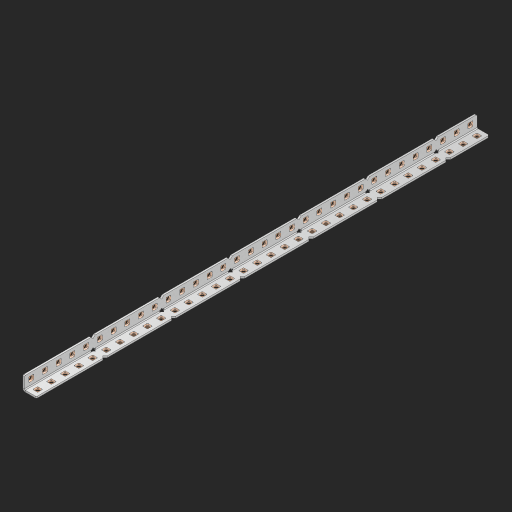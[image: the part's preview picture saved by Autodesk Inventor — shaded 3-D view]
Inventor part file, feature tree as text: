
AUTODESK INVENTOR PART (.ipt)
format: ipt  version: 2023 (Build 270158000, 158)  size: 1,092,096 bytes
history: native  units: in
note: dims shown in document units (in); Inventor stores cm internally (conversion verified against a paired STEP export)
features: other x72, extrude x67, sheet_metal_op x8, sketch x5, pattern_linear x1, mirror x1, chamfer x1
ambient origin geometry x8: Origin, YZ Plane, XZ Plane, XY Plane, X Axis, Y Axis, Z Axis, Center Point
bodies: Solid1 (feature_tree), Body (feature_tree)
feature tree (155):
  sheet_metal_op  "Flanges"
  sheet_metal_op  "Body Pattern"
  other  "Arc Length"
  pattern_linear  "Notch Pattern"  Spacing1=0.125in  [1 undecoded]
  other  "Diagonal Plane"
  mirror  "Everything Mirrored"
  chamfer  "End Chamfer"
  sketch  "Sketch1"  dims[d0=0.5in]
  other  "Plate1"
  sketch  "Sketch2"  dims[d1=16.5in]
  other  "Plate2"
  sheet_metal_op  "Bend1"
  sheet_metal_op  "Corner1"
  sketch  "Sketch8"  dims[d2=0.0625in]
  sketch  "Sketch9"  dims[d3=0.0625in]
  other  "Srf91"
  sheet_metal_op  "Body Pattern Sketch"
  other  "Srf92"
  sketch  "Sketch13"  dims[d4=0.0312in d5=0.125in d6=0.0625in d7=0.5in d8=90.0deg d9=0.0312in d10=0.25in d11=0.0625in d12=0.0625in d49=0.182in d50=0.02in d52=0.25in d53=0.0625in d54=0.0in d55=0.172in d56=1.0in d57=0.0in d85=0.1473in d86=0.1782in d89=0.0625in d90=0.0in d91=0.04in d92=0.0491in d95=2.5in d96=0.04in d97=0.25in d98=45.0deg d123=0.204in d126=0.0491in d127=0.1473in d128=0.08in d129=0.04in d130=2.5in d131=12.9921in d133=0.5in d134=0.3937in d136=1.0in]
  other  "Srf856"
  other  "Srf857"
  other  "Srf858"
  other  "Srf859"
  other  "Srf860"
  other  "Srf861"
  other  "Srf1275"
  other  "Srf1276"
  other  "Srf1278"
  other  "Srf1279"
  other  "Srf1280"
  other  "Srf1281"
  other  "Srf1282"
  other  "Srf1283"
  other  "Srf1383"
  other  "Srf1384"
  other  "Srf1385"
  other  "Srf1386"
  other  "Srf1387"
  other  "Srf1388"
  other  "Srf1389"
  other  "Srf1390"
  other  "Srf1391"
  other  "Srf1392"
  other  "Srf1393"
  other  "Srf1394"
  other  "Srf1395"
  other  "Srf1396"
  other  "Srf1397"
  other  "Srf1398"
  other  "Srf1399"
  other  "Srf1400"
  other  "Srf1401"
  other  "Srf1402"
  other  "Srf1403"
  other  "Srf1404"
  other  "Srf1405"
  other  "Srf1406"
  other  "Srf1407"
  other  "Srf1408"
  other  "Srf1475"
  other  "Srf1476"
  other  "Srf1477"
  other  "Srf1478"
  other  "Srf1479"
  other  "Srf1480"
  other  "Srf1481"
  other  "Srf1482"
  other  "Srf1483"
  other  "Srf1484"
  other  "Srf1485"
  other  "Srf1486"
  other  "Srf1487"
  other  "Srf1488"
  other  "Srf1489"
  other  "Srf1490"
  other  "Srf1491"
  other  "Srf1492"
  other  "Srf1493"
  other  "Srf1494"
  other  "Srf1495"
  other  "Srf1496"
  other  "Srf1497"
  other  "Srf1498"
  other  "Srf1499"
  other  "Srf1500"
  sheet_metal_op  "Body Stamp"
  sheet_metal_op  "Body Circle"
  sheet_metal_op  "Notch"
  extrude  "ExtrusionSrf92"  Depth=0.0625in
  extrude  "ExtrusionSrf856"  Depth=0.5in TaperAngle=90.0deg
  extrude  "ExtrusionSrf857"  Depth=0.25in
  extrude  "ExtrusionSrf858"  Depth=0.0625in
  extrude  "ExtrusionSrf859"  Depth=0.0625in
  extrude  "ExtrusionSrf860"  Depth=0.3937in
  extrude  "ExtrusionSrf861"  Depth=0.02in
  extrude  "ExtrusionSrf1275"  Depth=0.25in
  extrude  "ExtrusionSrf1276"  Depth=0.0625in
  extrude  "ExtrusionSrf1277"  TaperAngle=0.0deg  [1 undecoded]
  extrude  "ExtrusionSrf1278"  Depth=0.3937in
  extrude  "ExtrusionSrf1279"  Depth=0.3937in TaperAngle=0.0deg
  extrude  "ExtrusionSrf1280"  Depth=0.3937in
  extrude  "ExtrusionSrf1281"  Depth=0.3937in
  extrude  "ExtrusionSrf1282"  Depth=0.0625in
  extrude  "ExtrusionSrf1383"  Depth=0.3937in TaperAngle=0.0deg
  extrude  "ExtrusionSrf1384"  Depth=0.3937in
  extrude  "ExtrusionSrf1385"  Depth=0.25in TaperAngle=45.0deg
  extrude  "ExtrusionSrf1386"  Depth=0.3937in
  extrude  "ExtrusionSrf1387"  Depth=0.3937in
  extrude  "ExtrusionSrf1388"  Depth=0.3937in
  extrude  "ExtrusionSrf1389"  Depth=0.3937in
  extrude  "ExtrusionSrf1390"  Depth=0.3937in
  extrude  "ExtrusionSrf1391"  Depth=0.3937in
  extrude  "ExtrusionSrf1392"  Depth=0.3937in
  extrude  "ExtrusionSrf1393"  Depth=0.5in
  extrude  "ExtrusionSrf1394"  [1 undecoded]
  extrude  "ExtrusionSrf1395"  [1 undecoded]
  extrude  "ExtrusionSrf1396"  [1 undecoded]
  extrude  "ExtrusionSrf1397"  [1 undecoded]
  extrude  "ExtrusionSrf1398"  [1 undecoded]
  extrude  "ExtrusionSrf1399"  [1 undecoded]
  extrude  "ExtrusionSrf1400"  [1 undecoded]
  extrude  "ExtrusionSrf1401"  [1 undecoded]
  extrude  "ExtrusionSrf1402"  [1 undecoded]
  extrude  "ExtrusionSrf1403"  [1 undecoded]
  extrude  "ExtrusionSrf1404"  [1 undecoded]
  extrude  "ExtrusionSrf1405"  [1 undecoded]
  extrude  "ExtrusionSrf1406"  [1 undecoded]
  extrude  "ExtrusionSrf1407"  [1 undecoded]
  extrude  "ExtrusionSrf1408"  [1 undecoded]
  extrude  "ExtrusionSrf1475"  [1 undecoded]
  extrude  "ExtrusionSrf1476"  [1 undecoded]
  extrude  "ExtrusionSrf1477"  [1 undecoded]
  extrude  "ExtrusionSrf1478"  [1 undecoded]
  extrude  "ExtrusionSrf1479"  [1 undecoded]
  extrude  "ExtrusionSrf1480"  [1 undecoded]
  extrude  "ExtrusionSrf1481"  [1 undecoded]
  extrude  "ExtrusionSrf1482"  [1 undecoded]
  extrude  "ExtrusionSrf1483"  [1 undecoded]
  extrude  "ExtrusionSrf1484"  [1 undecoded]
  extrude  "ExtrusionSrf1485"  [1 undecoded]
  extrude  "ExtrusionSrf1486"  [1 undecoded]
  extrude  "ExtrusionSrf1487"  [1 undecoded]
  extrude  "ExtrusionSrf1488"  [1 undecoded]
  extrude  "ExtrusionSrf1489"  [1 undecoded]
  extrude  "ExtrusionSrf1490"  [1 undecoded]
  extrude  "ExtrusionSrf1491"  [1 undecoded]
  extrude  "ExtrusionSrf1492"  [1 undecoded]
  extrude  "ExtrusionSrf1493"  [1 undecoded]
  extrude  "ExtrusionSrf1494"  [1 undecoded]
  extrude  "ExtrusionSrf1495"  [1 undecoded]
  extrude  "ExtrusionSrf1496"  [1 undecoded]
  extrude  "ExtrusionSrf1497"  [1 undecoded]
  extrude  "ExtrusionSrf1498"  [1 undecoded]
  extrude  "ExtrusionSrf1499"  [1 undecoded]
  extrude  "ExtrusionSrf1500"  [1 undecoded]
note: 43 required parameter values undecoded (feature->parameter linkage not recoverable at this tier; creation-order binding heuristic only, values carry confidence <= 0.55)
